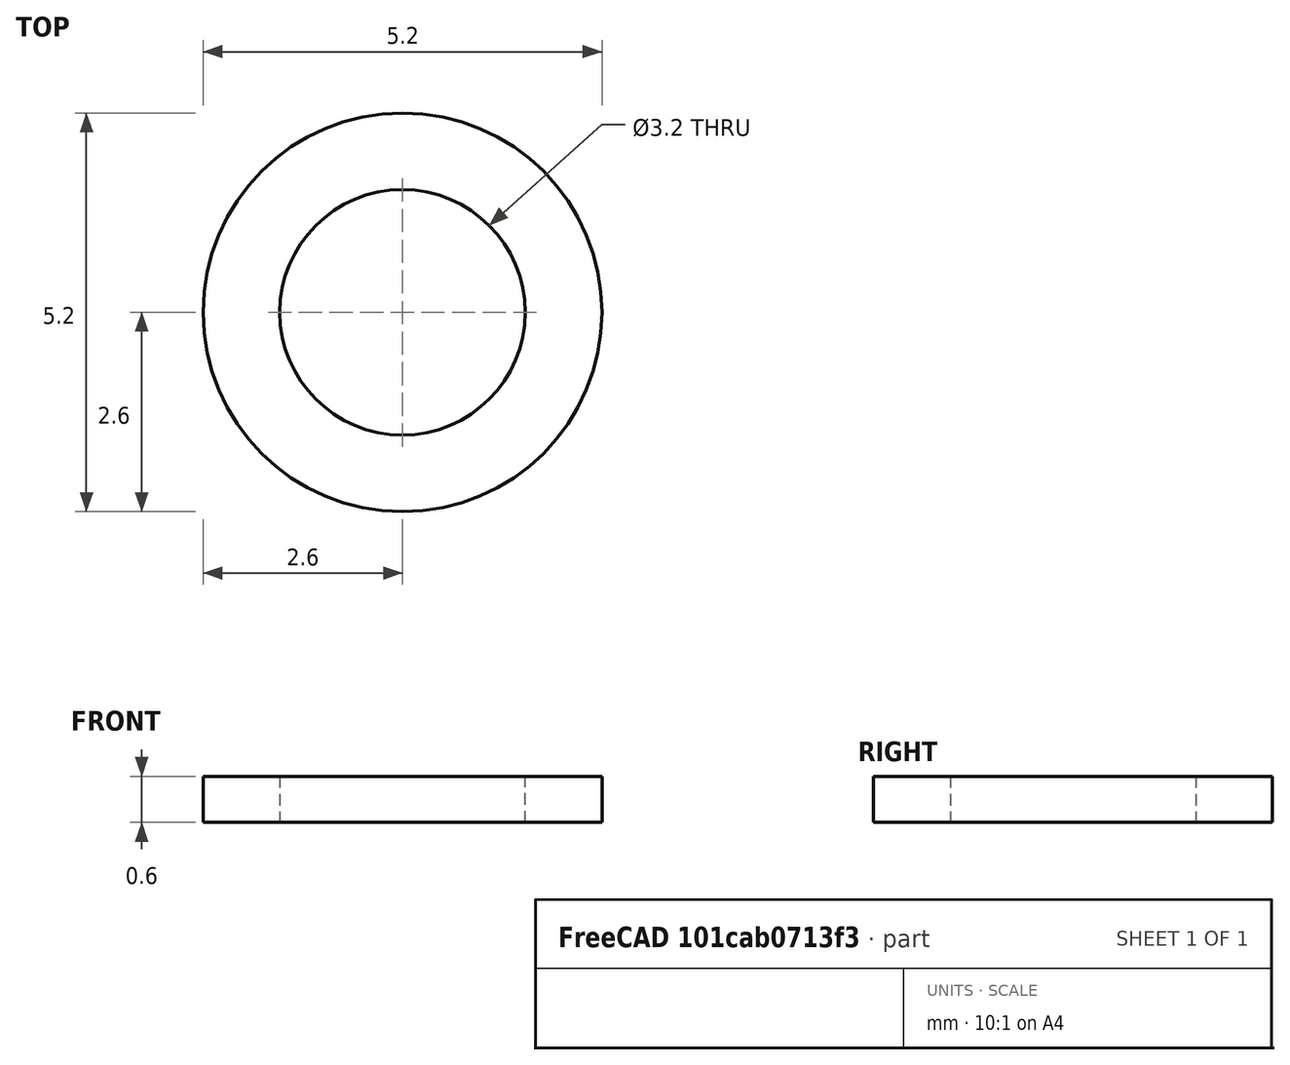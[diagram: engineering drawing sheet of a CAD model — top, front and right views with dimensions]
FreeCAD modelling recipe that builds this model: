
FCSTD DOCUMENT  (FreeCAD 0.18.1R)
Label: Spacer
License: All rights reserved
LicenseURL: http://en.wikipedia.org/wiki/All_rights_reserved
objects: Sketcher::SketchObject×1, PartDesign::Pad×1, PartDesign::Body×1, Spreadsheet::Sheet×1
note: 4 computed .brp shape members not serialized (recipe doc carries the construction recipe); baked Part::Feature solids carry a one-line shape summary decoded from their .brp

FEATURE [Sketcher::SketchObject] Sketch  label="Sketch Spacer Extrude"
  MapMode = 5
  Support = -> [XY_Plane]
  expr: Constraints[2] = Screws.m3D + 2mm
  expr: Constraints[3] = Screws.m3D
  sketch-geometry (2):
    g0: Circle CenterX=0 CenterY=0 CenterZ=0 NormalX=0 NormalY=0 NormalZ=1 AngleXU=0 Radius=1.6
    g1: Circle CenterX=0 CenterY=0 CenterZ=0 NormalX=0 NormalY=0 NormalZ=1 AngleXU=0 Radius=2.6
  constraints (4):
    c: Coincident(g0,g-1)
    c: Coincident(g1,g0)
    c: Diameter(g1) = 5.2
    c: Diameter(g0) = 3.2
FEATURE [PartDesign::Pad] Pad  label="Spacer Extrude"
  Length = 0.6
  Length2 = 100
  Profile = -> Sketch
  Type = 0
FEATURE [PartDesign::Body] Body  label="Spacer"
  Group = -> [Sketch,Pad]
  Origin = -> Origin
  Tip = -> Pad
FEATURE [Spreadsheet::Sheet] Spreadsheet  label="Screws"
  cells = A1=Screw Type; B1=Length; D1=Diameter Loose; F1=Diameter Tight; A2=M3 Tapping; B2=m3tl; C2(m3tl)==11mm; D2=m3tD; E2(m3tD)==3.4mm; F2=m3td; G2(m3td)==2.8mm; A3=M3; B3=m3l; C3(m3l)==30mm; D3=m3D; E3(m3D)==3.2mm; F3=m3d; G3(m3d)==2.8mm
